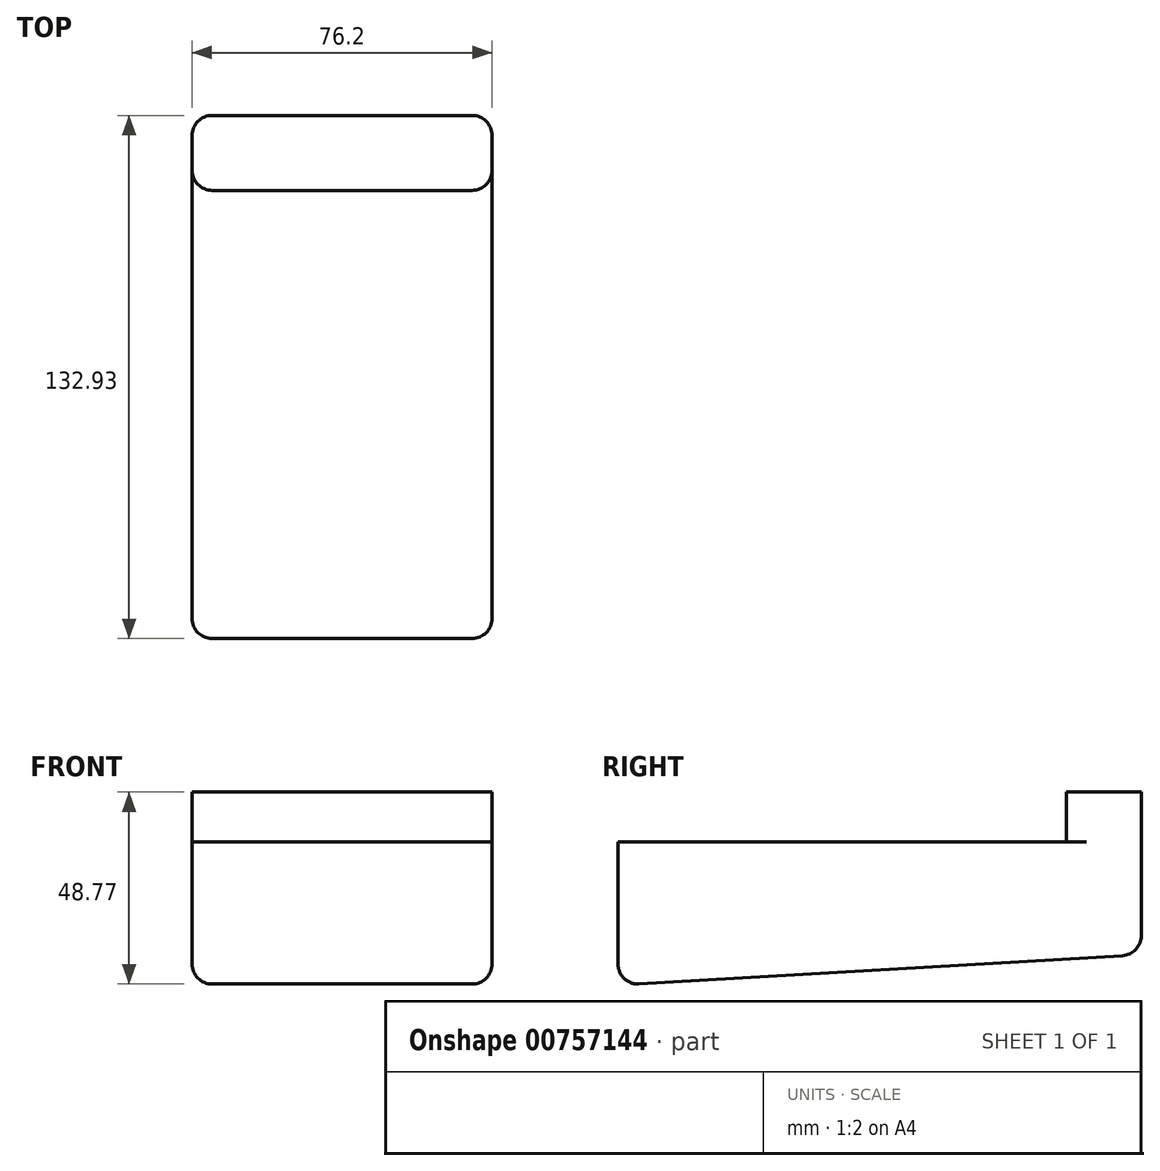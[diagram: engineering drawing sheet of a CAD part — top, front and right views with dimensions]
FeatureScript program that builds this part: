
annotation { "Feature Type Name" : "Feature", "Feature Type Description" : "" }
export const myFeature = defineFeature(function(context is Context, id is Id, definition is map)
    precondition{}
    {
        {
            var Q0;
            Q0=qCreatedBy(makeId("Right.planeOp"),FACE);
            cPlane(context, id + "F0", {"entities" : qUnion([Q0]), "cplaneType" : CPlaneType.OFFSET, "offset" : 76.2 * mm, "width" : 152.4 * mm, "height" : 152.4 * mm});
        }
        {
            var Q0;
            Q0=qCreatedBy(id+"F0.planeOp",FACE);
            var sketch = newSketch(context, id + "F1", { "sketchPlane" : qUnion([Q0])});
            skLineSegment(sketch, "E0.bottom", {"start": v(0, 0) * mm, "end": v(-19.05, 0) * mm});
            skLineSegment(sketch, "E0.left", {"start": v(0, 0) * mm, "end": v(0, -41.28) * mm});
            skLineSegment(sketch, "E0.right", {"start": v(-19.05, 0) * mm, "end": v(-19.05, -12.7) * mm});
            skLineSegment(sketch, "E1.top", {"start": v(-19.05, -12.7) * mm, "end": v(-132.93, -12.7) * mm});
            skLineSegment(sketch, "E2", {"start": v(0, -41.28) * mm, "end": v(-132.93, -49.08) * mm});
            skPoint(sketch, "E3.end.orphan", {"position": v(-107.95, -47.61) * mm});
            skLineSegment(sketch, "E4", {"start": v(-132.93, -12.7) * mm, "end": v(-132.93, -49.08) * mm});
            skSolve(sketch);
        }
        {
            var Q0;
            Q0=makeQuery(id+"F1.imprint","IMPRINT",FACE,{"disambiguationData":[TD([[makeQuery(id+"F1.imprint","IMPRINT",EDGE,{"derivedFrom":sQuery(id+"F1.wireOp",EDGE,"E0.bottom")}),1.0]])]});
            extrude(context, id + "F2", {"entities" : qUnion([Q0]), "oppositeDirection" : true, "depth" : 76.2 * mm, "offsetDistance" : 25.4 * mm});
        }
        {
            var Q0;
            Q0=makeQuery(id+"F2.opExtrude","SWEPT_EDGE",EDGE,{"disambiguationData":[OSD([sQuery(id+"F1.wireOp",EDGE,"E0.left"),sQuery(id+"F1.wireOp",EDGE,"E2")])]});
            var Q1;
            Q1=makeQuery(id+"F2.opExtrude","CAP_EDGE",EDGE,{"disambiguationData":[OSD([sQuery(id+"F1.wireOp",EDGE,"E0.left")])],"isStart":true});
            var Q2;
            Q2=makeQuery(id+"F2.opExtrude","CAP_EDGE",EDGE,{"disambiguationData":[OSD([sQuery(id+"F1.wireOp",EDGE,"E0.left")])],"isStart":false});
            var Q3;
            Q3=makeQuery(id+"F2.opExtrude","CAP_EDGE",EDGE,{"disambiguationData":[OSD([sQuery(id+"F1.wireOp",EDGE,"E2")])],"isStart":true});
            var Q4;
            Q4=makeQuery(id+"F2.opExtrude","CAP_EDGE",EDGE,{"disambiguationData":[OSD([sQuery(id+"F1.wireOp",EDGE,"E2")])],"isStart":false});
            var Q5;
            Q5=makeQuery(id+"F2.opExtrude","SWEPT_EDGE",EDGE,{"disambiguationData":[OSD([sQuery(id+"F1.wireOp",EDGE,"E3"),sQuery(id+"F1.wireOp",EDGE,"E2")])]});
            var Q6;
            Q6=makeQuery(id+"F2.opExtrude","CAP_EDGE",EDGE,{"disambiguationData":[OSD([sQuery(id+"F1.wireOp",EDGE,"E1.right"),sQuery(id+"F1.wireOp",EDGE,"E3")])],"isStart":false});
            var Q7;
            Q7=makeQuery(id+"F2.opExtrude","CAP_EDGE",EDGE,{"disambiguationData":[OSD([sQuery(id+"F1.wireOp",EDGE,"E1.right"),sQuery(id+"F1.wireOp",EDGE,"E3")])],"isStart":true});
            var Q8;
            Q8=makeQuery(id+"F2.opExtrude","CAP_EDGE",EDGE,{"disambiguationData":[OSD([sQuery(id+"F1.wireOp",EDGE,"E0.right")])],"isStart":false});
            var Q9;
            Q9=makeQuery(id+"F2.opExtrude","CAP_EDGE",EDGE,{"disambiguationData":[OSD([sQuery(id+"F1.wireOp",EDGE,"E0.right")])],"isStart":true});
            var Q10;
            Q10=makeQuery(id+"F2.opExtrude","CAP_EDGE",EDGE,{"disambiguationData":[OSD([sQuery(id+"F1.wireOp",EDGE,"E4")])],"isStart":false});
            var Q11;
            Q11=makeQuery(id+"F2.opExtrude","CAP_EDGE",EDGE,{"disambiguationData":[OSD([sQuery(id+"F1.wireOp",EDGE,"E4")])],"isStart":true});
            fillet(context, id + "F3", {"entities" : qUnion([Q0, Q1, Q2, Q3, Q4, Q5, Q6, Q7, Q8, Q9, Q10, Q11]), "radius" : 5.08 * mm, "tangentPropagation" : true, "allowEdgeOverflow" : false});
        }
    });
